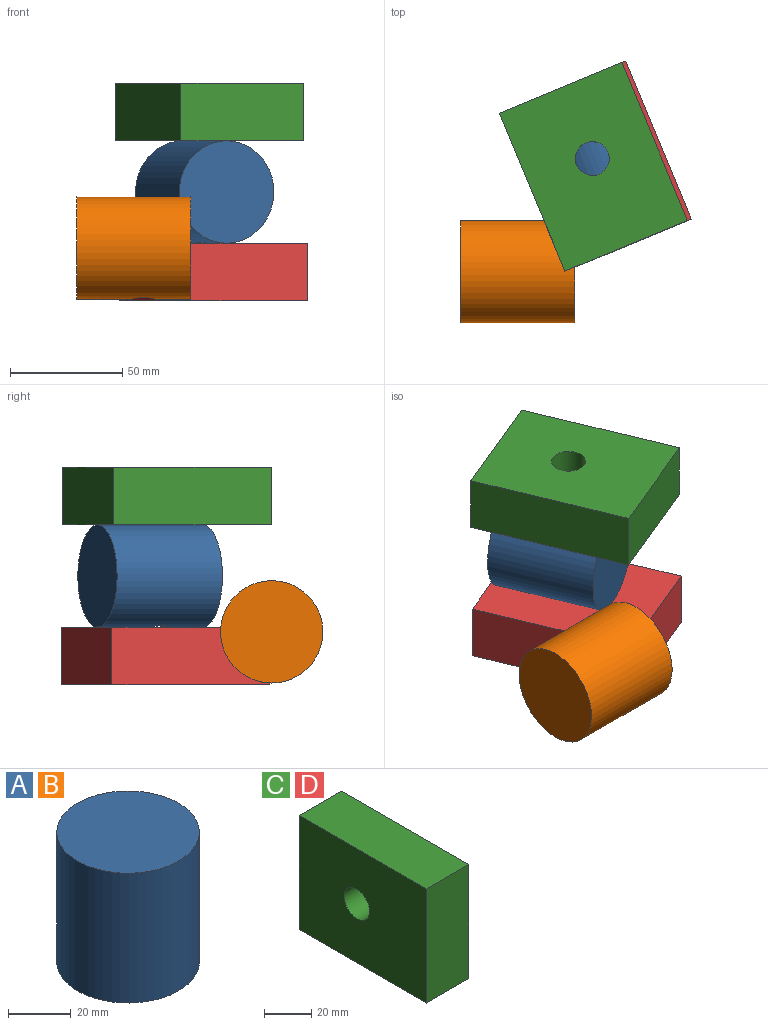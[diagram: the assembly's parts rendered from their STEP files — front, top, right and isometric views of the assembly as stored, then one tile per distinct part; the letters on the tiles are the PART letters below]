
ASSEMBLY  parts=4 mates=1
PART A: 5 faces, bbox 45.6x45.6x50.8 mm
  f0: cylinder r=22.79mm len=50.8mm, axis (0,0,-1), area 7183.6mm2, adj f1,f2,f3
  f1: plane 45.59x45.59mm, normal (0,0,1), area 1632.2mm2, adj f0
  f2: plane 45.59x45.59mm, normal (0,0,-1), area 1632.2mm2, adj f0
  f3: cylinder r=5.38mm len=22.79mm, axis (-1,0,0), area 760.3mm2, adj f0,f4
  f4: plane 10.77x10.77mm, normal (1,0,0), area 91.1mm2, adj f3
PART B: same geometry as A
PART C: 7 faces, bbox 25.4x76.1x59 mm
  f0: plane 76.14x25.4mm, normal (0,0,1), area 1933.9mm2, adj f1,f3,f4,f5
  f1: plane 59.05x25.4mm, normal (0,-1,0), area 1499.8mm2, adj f0,f2,f4,f5
  f2: plane 76.14x25.4mm, normal (0,0,-1), area 1933.9mm2, adj f1,f3,f4,f5
  f3: plane 59.05x25.4mm, normal (0,1,0), area 1499.8mm2, adj f0,f2,f4,f5
  f4: plane 76.14x59.05mm, normal (1,0,0), area 4315.8mm2, adj f0,f1,f2,f3,f6
  f5: plane 76.14x59.05mm, normal (-1,0,0), area 4315.8mm2, adj f0,f1,f2,f3,f6
  f6: cylinder r=7.57mm len=25.4mm, axis (1,0,0), area 1207.9mm2, adj f4,f5
PART D: same geometry as C
PLACE A rot(axis=(0.49,0.73,-0.49),108deg) t=(-94.65,89.46,50.82)mm
PLACE B rot(axis=(0,1,0),90deg) t=(-141.95,11.85,25.95)mm
PLACE C rot(axis=(-0.19,0.96,0.19),92.2deg) t=(-80.45,55.22,99.16)mm
PLACE D rot(axis=(0.19,-0.96,0.19),92.2deg) t=(-80.45,55.22,2.48)mm
MATE revolute A.f3 <-> D.f6  axis (0,0,-1) through (-83.32,62.13,27.88)mm
